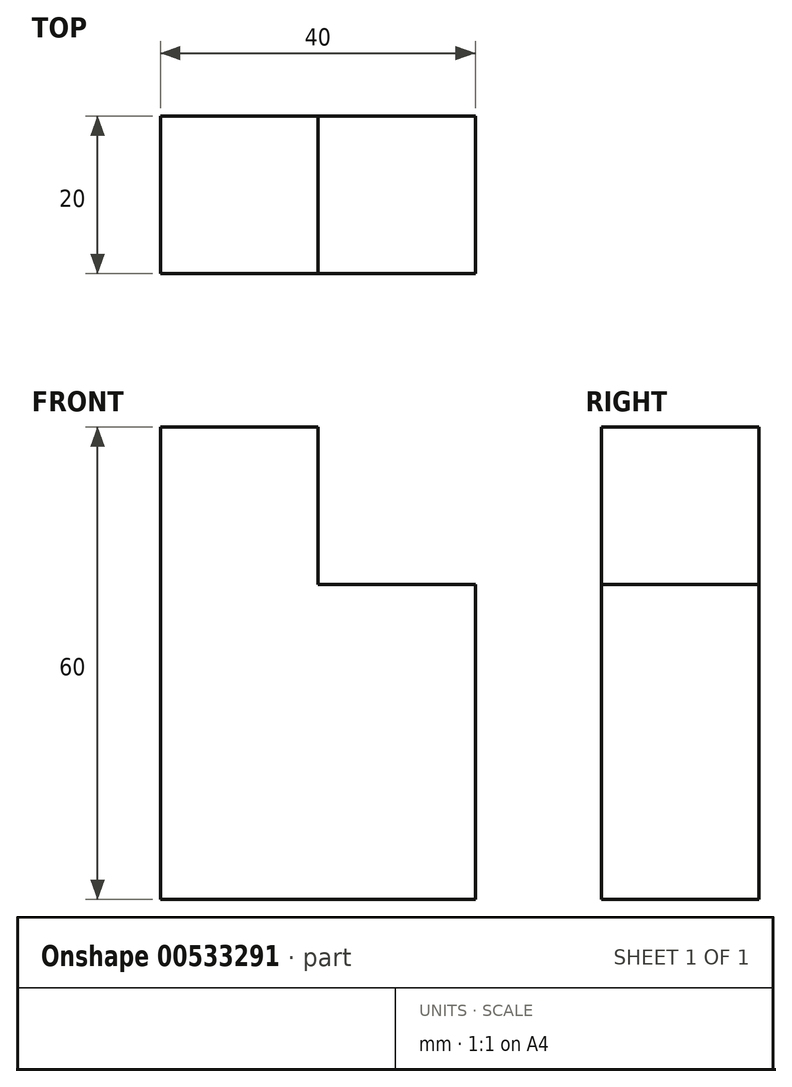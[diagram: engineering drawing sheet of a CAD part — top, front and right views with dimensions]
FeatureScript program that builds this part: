
annotation { "Feature Type Name" : "Feature", "Feature Type Description" : "" }
export const myFeature = defineFeature(function(context is Context, id is Id, definition is map)
    precondition{}
    {
        {
            var Q0;
            Q0=qCreatedBy(makeId("Front.planeOp"),FACE);
            var sketch = newSketch(context, id + "F0", { "sketchPlane" : qUnion([Q0])});
            skLineSegment(sketch, "E0", {"start": v(-69.62, 38.11) * mm, "end": v(-69.62, 60) * mm});
            skLineSegment(sketch, "E1", {"start": v(-69.62, 60) * mm, "end": v(-49.62, 60) * mm});
            skLineSegment(sketch, "E2", {"start": v(-49.62, 60) * mm, "end": v(-49.62, 40) * mm});
            skLineSegment(sketch, "E3", {"start": v(-49.62, 40) * mm, "end": v(-29.62, 40) * mm});
            skLineSegment(sketch, "E4", {"start": v(-29.62, 40) * mm, "end": v(-29.62, 0) * mm});
            skLineSegment(sketch, "E5", {"start": v(-29.62, 0) * mm, "end": v(-69.62, 0) * mm});
            skLineSegment(sketch, "E6", {"start": v(-69.62, 0) * mm, "end": v(-69.62, 60) * mm});
            skSolve(sketch);
        }
        {
            var Q0;
            Q0 = qSketchRegion(id + "F0", true);
            extrude(context, id + "F1", {"entities" : qUnion([Q0]), "depth" : 20 * mm, "offsetDistance" : 25 * mm});
        }
    });
